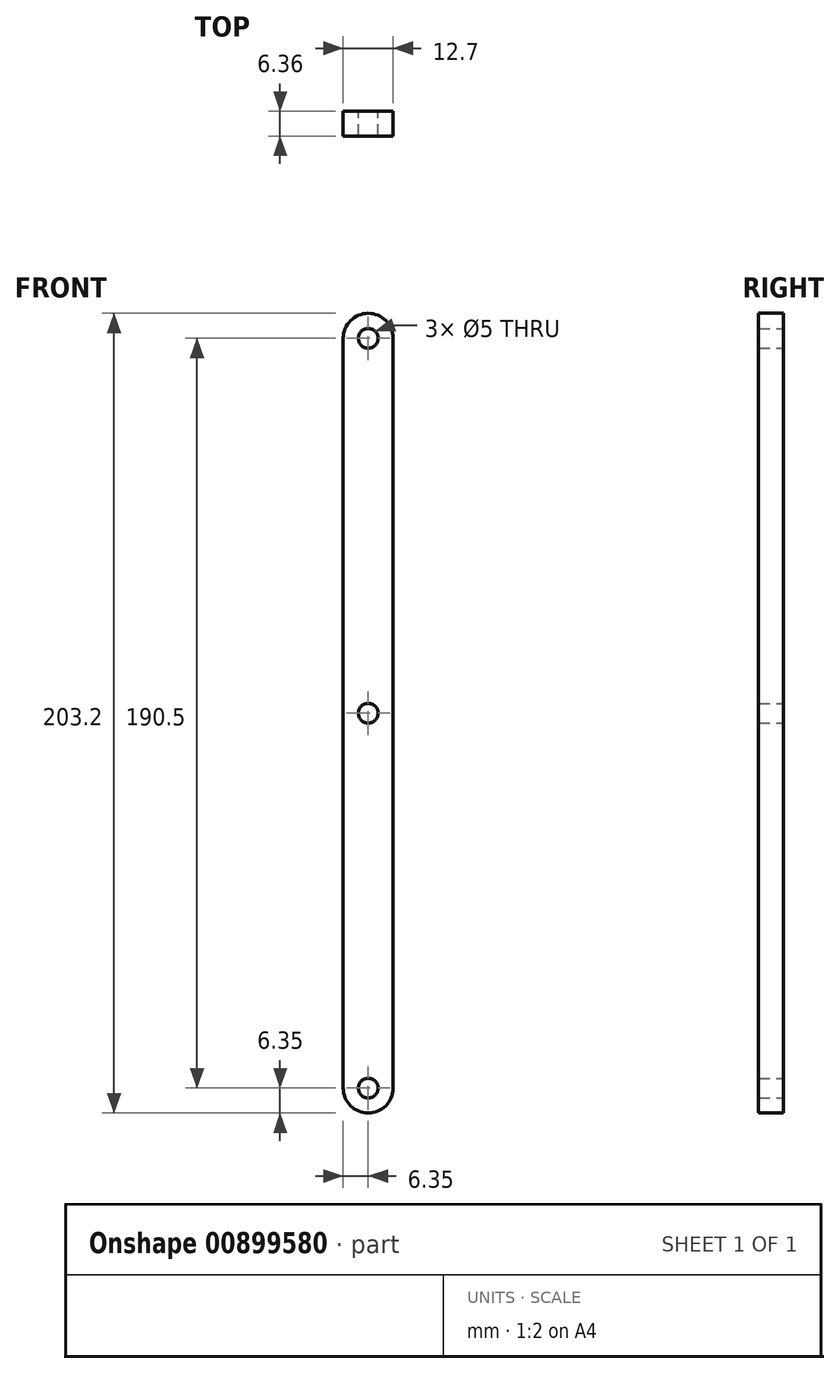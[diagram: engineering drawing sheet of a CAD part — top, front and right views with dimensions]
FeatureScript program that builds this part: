
annotation { "Feature Type Name" : "Feature", "Feature Type Description" : "" }
export const myFeature = defineFeature(function(context is Context, id is Id, definition is map)
    precondition{}
    {
        {
            var Q0;
            Q0=qCreatedBy(makeId("Front.planeOp"),FACE);
            var sketch = newSketch(context, id + "F0", { "sketchPlane" : qUnion([Q0])});
            skLineSegment(sketch, "E0", {"start": v(0, 95.25) * mm, "end": v(0, -95.25) * mm});
            skLineSegment(sketch, "E1", {"start": v(12.7, 95.25) * mm, "end": v(12.7, -95.25) * mm});
            skArc(sketch, "E2", {"start": v(12.7, 95.25) * mm, "mid": v(6.35, 101.6) * mm, "end": v(0, 95.25) * mm});
            skArc(sketch, "E3", {"start": v(0, -95.25) * mm, "mid": v(6.35, -101.6) * mm, "end": v(12.7, -95.25) * mm});
            skCircle(sketch, "E4", {"center": v(6.35, -95.25) * mm, "radius": 2.5 * mm});
            skCircle(sketch, "E5", {"center": v(6.35, 95.25) * mm, "radius": 2.5 * mm});
            skLineSegment(sketch, "E6", {"start": v(0, 0) * mm, "end": v(12.7, 0) * mm});
            skCircle(sketch, "E7", {"center": v(6.35, 0) * mm, "radius": 2.5 * mm});
            skSolve(sketch);
        }
        {
            var Q0;
            {var subQ0=sQuery(id+"F0.wireOp",EDGE,"E2");Q0=makeQuery(id+"F0.imprint","IMPRINT",FACE,{"disambiguationData":[TD([[makeQuery(id+"F0.imprint","IMPRINT",EDGE,{"derivedFrom":subQ0}),1.0]])]});}
            var Q1;
            {var subQ0=sQuery(id+"F0.wireOp",EDGE,"E3");Q1=makeQuery(id+"F0.imprint","IMPRINT",FACE,{"disambiguationData":[TD([[makeQuery(id+"F0.imprint","IMPRINT",EDGE,{"derivedFrom":subQ0}),1.0]])]});}
            extrude(context, id + "F1", {"entities" : qUnion([Q0, Q1]), "endBound" : BoundingType.SYMMETRIC, "depth" : 6.35 * mm, "offsetDistance" : 25.4 * mm});
        }
    });
